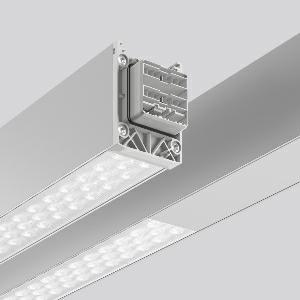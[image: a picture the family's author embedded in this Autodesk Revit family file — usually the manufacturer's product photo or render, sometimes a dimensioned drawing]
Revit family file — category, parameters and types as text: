
# Revit family: linedo_4_5m_30_11001100_954530_840_400_502_ee97
name_source: partatom
category: Lighting Fixtures
units: mm (PartAtom-declared; Revit-internal decimal feet)

## family parameters
Cut with Voids When Loaded = No
Host = Face
Light Source = No
Part Type = Normal
Room Calculation Point = No
Round Connector Dimension = Use Diameter
Shared = No

## types (1)
- LINEDO_4,5m_30_11001100 (1 x LED Modul 840, 3400 lm, 4000)
    Apparent Load = 84 VA
    CIE Flux Codes = 89 97 99 100 100
    Color Rendering = 80
    Color Temperature = 4000
    Default Elevation = 1800 mm
    Description = LINEDO, 84 W, 13600 lm, 840, aluminium, on/off
Continuous line luminaire, L 4547 B 58 H 76
    Height = 76 mm
    Lamp = 1 x LED Modul 840
    Lamp Light Flux = 3400 lm
    Lamp count = 1
    Length = 4547 mm
    Lifetime = 50000 h
    Luminous efficacy = 162 lm/W
    Manufacturer = RZB
    ModVariant = No
    Model = 954530.840.400.502
    Mounting Place = Ceiling
    Mounting Type = Surface mounted, Pendant
    Number of Poles = 1
    OnlyDefault = Yes
    Power Factor = 1
    Product Name = LINEDO_4,5m_30_11001100
    Product group = Surface mounted continuous line luminaire system
    ProductGroupID = 310
    Protection Class = Protection class I
    Protection Degree = IP 54
    RLX_Detail_Level = 1
    RLX_Emergency_Light_Flux = 0 lm
    RLX_Emergency_Type = 0
    RLX_Emergency_Type_DB = No
    RlxData = <blob elided: 52557 chars, md5=928d46fa>
    Socket = socket
    Standby Power = 0 W
    System Light Flux = 13600 lm
    System Power = 84 W
    Type Comments = Product without accessories
    Type Image = 954530.850.476.504.jpg
    URL = http://relux.com
    VarID = ---
    Voltage = 230 V
    Voltage Range = 220-240 V
    Weight = 0.00 kg
    Width = 58 mm

## geometry (parser evidence)
native form markers: Blend x4, Sweep x21
no freeform markers — native parametric forms only
